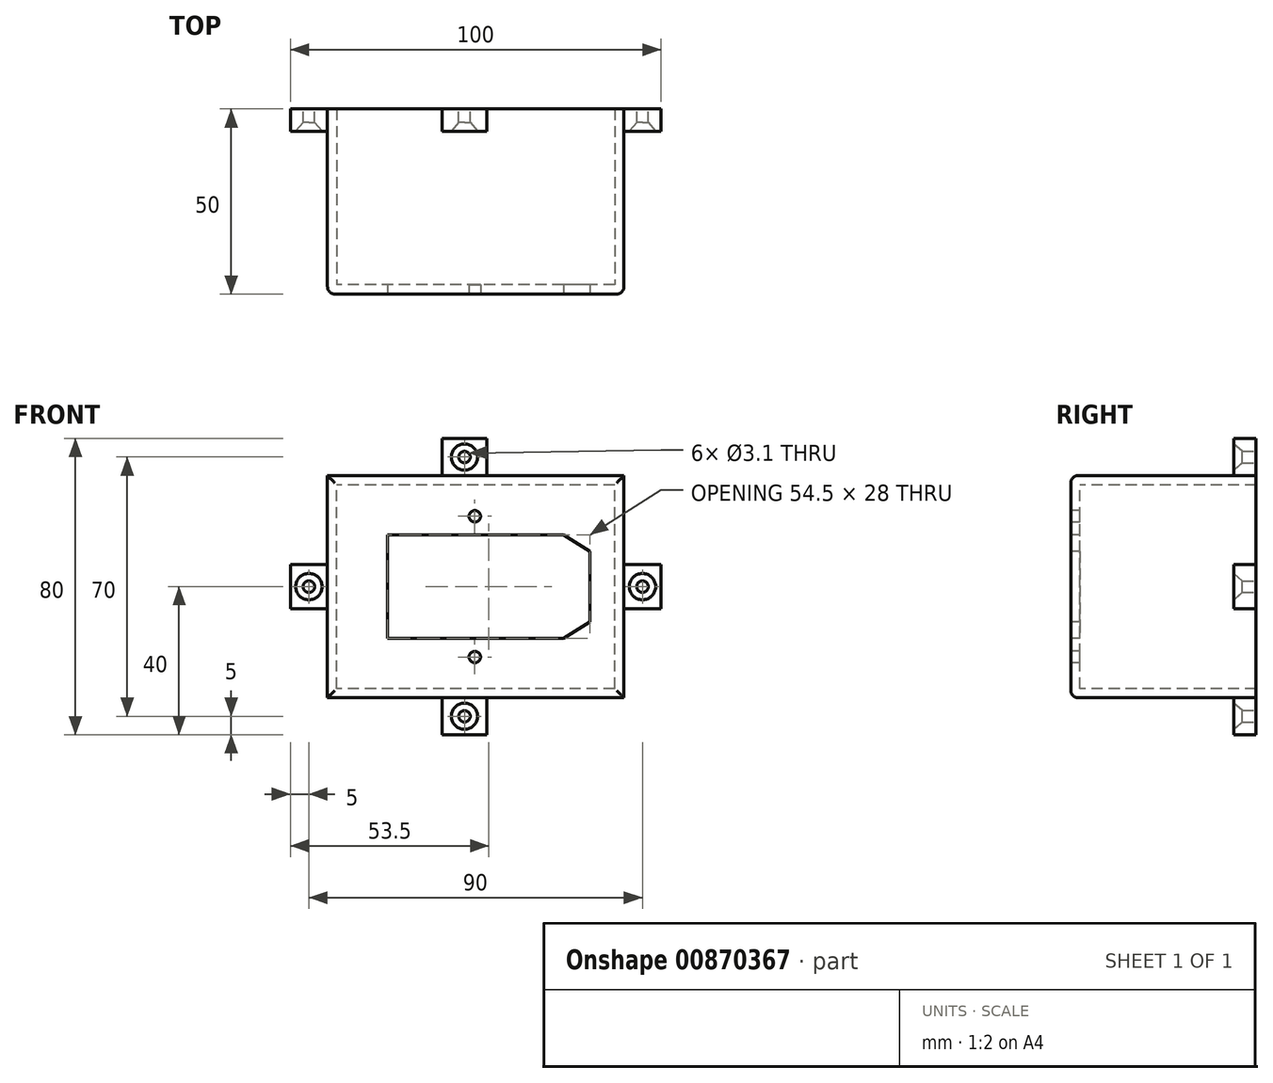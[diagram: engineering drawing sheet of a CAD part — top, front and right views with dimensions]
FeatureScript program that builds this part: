
annotation { "Feature Type Name" : "Feature", "Feature Type Description" : "" }
export const myFeature = defineFeature(function(context is Context, id is Id, definition is map)
    precondition{}
    {
        {
            var Q0;
            Q0=qCreatedBy(makeId("Front.planeOp"),FACE);
            var sketch = newSketch(context, id + "F0", { "sketchPlane" : qUnion([Q0])});
            skLineSegment(sketch, "E0.bottom", {"start": v(40, -30) * mm, "end": v(-40, -30) * mm});
            skLineSegment(sketch, "E0.top", {"start": v(40, 30) * mm, "end": v(-40, 30) * mm});
            skLineSegment(sketch, "E0.left", {"start": v(40, -30) * mm, "end": v(40, 30) * mm});
            skLineSegment(sketch, "E0.right", {"start": v(-40, -30) * mm, "end": v(-40, 30) * mm});
            skPoint(sketch, "E0.middle", {"position": v(0, 0) * mm});
            skLineSegment(sketch, "E1.bottom", {"start": v(23.75, -14) * mm, "end": v(-23.75, -14) * mm});
            skLineSegment(sketch, "E1.top", {"start": v(23.75, 14) * mm, "end": v(-23.75, 14) * mm});
            skLineSegment(sketch, "E1.left", {"start": v(23.75, -14) * mm, "end": v(23.75, 14) * mm});
            skLineSegment(sketch, "E1.right", {"start": v(-23.75, -14) * mm, "end": v(-23.75, 14) * mm});
            skLineSegment(sketch, "E2", {"start": v(30.75, 9.5) * mm, "end": v(30.75, -9.5) * mm});
            skLineSegment(sketch, "E3", {"start": v(30.75, -9.5) * mm, "end": v(23.75, -14) * mm});
            skLineSegment(sketch, "E4", {"start": v(30.75, 9.5) * mm, "end": v(23.75, 14) * mm});
            skLineSegment(sketch, "E5.0", {"start": v(37.5, -27.5) * mm, "end": v(-37.5, -27.5) * mm});
            skLineSegment(sketch, "E5.1", {"start": v(37.5, -27.5) * mm, "end": v(37.5, 27.5) * mm});
            skLineSegment(sketch, "E5.2", {"start": v(37.5, 27.5) * mm, "end": v(-37.5, 27.5) * mm});
            skLineSegment(sketch, "E5.3", {"start": v(-37.5, -27.5) * mm, "end": v(-37.5, 27.5) * mm});
            skCircle(sketch, "E6", {"center": v(-0.25, 19) * mm, "radius": 1.55 * mm});
            skPoint(sketch, "E6.centerSnap0", {"position": v(0, 14) * mm});
            skCircle(sketch, "E7.MirrorC", {"center": v(-0.25, -19) * mm, "radius": 1.55 * mm});
            skSolve(sketch);
        }
        {
            var Q0;
            Q0=qSketchRegion(id+"F0",true);
            extrude(context, id + "F1", {"entities" : qUnion([Q0]), "oppositeDirection" : true, "depth" : 50 * mm, "offsetDistance" : 25 * mm});
        }
        {
            var Q0;
            Q0=makeQuery(id+"F0.imprint","IMPRINT",FACE,{"disambiguationData":[TD([[makeQuery(id+"F0.imprint","IMPRINT",EDGE,{"derivedFrom":sQuery(id+"F0.wireOp",EDGE,"E1.bottom")}),1.0]])]});
            extrude(context, id + "F2", {"entities" : qUnion([Q0]), "operationType" : NewBodyOperationType.ADD, "oppositeDirection" : true, "depth" : 2.5 * mm, "offsetDistance" : 25 * mm});
        }
        {
            var Q0;
            Q0=makeQuery(id+"F1.opExtrude","CAP_FACE",FACE,{"disambiguationData":[OSD([sQuery(id+"F0.wireOp",EDGE,"E0.bottom"),sQuery(id+"F0.wireOp",EDGE,"E0.top"),sQuery(id+"F0.wireOp",EDGE,"E0.left"),sQuery(id+"F0.wireOp",EDGE,"E0.right"),sQuery(id+"F0.wireOp",EDGE,"E5.0"),sQuery(id+"F0.wireOp",EDGE,"E5.1"),sQuery(id+"F0.wireOp",EDGE,"E5.2"),sQuery(id+"F0.wireOp",EDGE,"E5.3")])],"isStart":false});
            var sketch = newSketch(context, id + "F3", { "sketchPlane" : qUnion([Q0])});
            skLineSegment(sketch, "E8.bottom", {"start": v(40, -6) * mm, "end": v(50, -6) * mm});
            skLineSegment(sketch, "E8.top", {"start": v(40, 6) * mm, "end": v(50, 6) * mm});
            skLineSegment(sketch, "E8.left", {"start": v(40, -6) * mm, "end": v(40, 6) * mm});
            skLineSegment(sketch, "E8.right", {"start": v(50, -6) * mm, "end": v(50, 6) * mm});
            skCircle(sketch, "E9", {"center": v(45, 0) * mm, "radius": 1.55 * mm});
            skLineSegment(sketch, "E10.MirrorCS", {"start": v(-50, -6) * mm, "end": v(-50, 6) * mm});
            skCircle(sketch, "E11.MirrorC", {"center": v(-45, 0) * mm, "radius": 1.55 * mm});
            skLineSegment(sketch, "E12.MirrorCS", {"start": v(-40, -6) * mm, "end": v(-50, -6) * mm});
            skLineSegment(sketch, "E13.MirrorCS", {"start": v(-40, -6) * mm, "end": v(-40, 6) * mm});
            skLineSegment(sketch, "E14.MirrorCS", {"start": v(-40, 6) * mm, "end": v(-50, 6) * mm});
            skLineSegment(sketch, "E15.bottom", {"start": v(-2.98, -40) * mm, "end": v(9.02, -40) * mm});
            skLineSegment(sketch, "E15.top", {"start": v(-2.98, -30) * mm, "end": v(9.02, -30) * mm});
            skLineSegment(sketch, "E15.left", {"start": v(-2.98, -40) * mm, "end": v(-2.98, -30) * mm});
            skLineSegment(sketch, "E15.right", {"start": v(9.02, -40) * mm, "end": v(9.02, -30) * mm});
            skCircle(sketch, "E16", {"center": v(3.02, -35) * mm, "radius": 1.55 * mm});
            skLineSegment(sketch, "E17.MirrorCS", {"start": v(9.02, 40) * mm, "end": v(9.02, 30) * mm});
            skLineSegment(sketch, "E18.MirrorCS", {"start": v(-2.98, 40) * mm, "end": v(-2.98, 30) * mm});
            skLineSegment(sketch, "E19.MirrorCS", {"start": v(-2.98, 40) * mm, "end": v(9.02, 40) * mm});
            skLineSegment(sketch, "E20.MirrorCS", {"start": v(-2.98, 30) * mm, "end": v(9.02, 30) * mm});
            skCircle(sketch, "E21.MirrorC", {"center": v(3.02, 35) * mm, "radius": 1.55 * mm});
            skSolve(sketch);
        }
        {
            var Q0;
            Q0=makeQuery(id+"F3.imprint","IMPRINT",FACE,{"disambiguationData":[TD([[makeQuery(id+"F3.imprint","IMPRINT",EDGE,{"derivedFrom":sQuery(id+"F3.wireOp",EDGE,"E8.bottom")}),1.0]])]});
            var Q1;
            Q1=makeQuery(id+"F3.imprint","IMPRINT",FACE,{"disambiguationData":[TD([[makeQuery(id+"F3.imprint","IMPRINT",EDGE,{"derivedFrom":sQuery(id+"F3.wireOp",EDGE,"E15.bottom")}),1.0]])]});
            var Q2;
            Q2=makeQuery(id+"F3.imprint","IMPRINT",FACE,{"disambiguationData":[TD([[makeQuery(id+"F3.imprint","IMPRINT",EDGE,{"derivedFrom":sQuery(id+"F3.wireOp",EDGE,"E13.MirrorCS")}),1.0]])]});
            var Q3;
            Q3=makeQuery(id+"F3.imprint","IMPRINT",FACE,{"disambiguationData":[TD([[makeQuery(id+"F3.imprint","IMPRINT",EDGE,{"derivedFrom":sQuery(id+"F3.wireOp",EDGE,"E17.MirrorCS")}),-1.0]])]});
            extrude(context, id + "F4", {"entities" : qUnion([Q0, Q1, Q2, Q3]), "operationType" : NewBodyOperationType.ADD, "oppositeDirection" : true, "depth" : 6 * mm, "offsetDistance" : 25 * mm});
        }
        {
            var Q0;
            Q0=makeQuery(id+"F1.opExtrude","CAP_EDGE",EDGE,{"disambiguationData":[OSD([sQuery(id+"F0.wireOp",EDGE,"E0.left")])],"isStart":true});
            var Q1;
            Q1=makeQuery(id+"F1.opExtrude","CAP_EDGE",EDGE,{"disambiguationData":[OSD([sQuery(id+"F0.wireOp",EDGE,"E0.right")])],"isStart":true});
            var Q2;
            Q2=makeQuery(id+"F1.opExtrude","CAP_EDGE",EDGE,{"disambiguationData":[OSD([sQuery(id+"F0.wireOp",EDGE,"E0.top")])],"isStart":true});
            var Q3;
            Q3=makeQuery(id+"F1.opExtrude","CAP_EDGE",EDGE,{"disambiguationData":[OSD([sQuery(id+"F0.wireOp",EDGE,"E0.bottom")])],"isStart":true});
            fillet(context, id + "F5", {"entities" : qUnion([Q0, Q1, Q2, Q3]), "radius" : 2 * mm, "tangentPropagation" : true, "allowEdgeOverflow" : false});
        }
        {
            var Q0;
            Q0=makeQuery(id+"F4.opExtrude","CAP_FACE",FACE,{"disambiguationData":[OSD([sQuery(id+"F3.wireOp",EDGE,"E15.bottom"),sQuery(id+"F3.wireOp",EDGE,"E15.top"),sQuery(id+"F3.wireOp",EDGE,"E15.left"),sQuery(id+"F3.wireOp",EDGE,"E15.right"),sQuery(id+"F3.wireOp",EDGE,"E16")])],"isStart":false});
            var sketch = newSketch(context, id + "F6", { "sketchPlane" : qUnion([Q0])});
            skPoint(sketch, "E22", {"position": v(-3.02, -35) * mm});
            skSolve(sketch);
        }
        {
            var Q0;
            Q0=makeQuery(id+"F4.opExtrude","CAP_FACE",FACE,{"disambiguationData":[OSD([sQuery(id+"F3.wireOp",EDGE,"E17.MirrorCS"),sQuery(id+"F3.wireOp",EDGE,"E18.MirrorCS"),sQuery(id+"F3.wireOp",EDGE,"E19.MirrorCS"),sQuery(id+"F3.wireOp",EDGE,"E20.MirrorCS"),sQuery(id+"F3.wireOp",EDGE,"E21.MirrorC")])],"isStart":false});
            var sketch = newSketch(context, id + "F7", { "sketchPlane" : qUnion([Q0])});
            skPoint(sketch, "E23", {"position": v(-3.02, 35) * mm});
            skSolve(sketch);
        }
        {
            var Q0;
            Q0=makeQuery(id+"F4.opExtrude","CAP_FACE",FACE,{"disambiguationData":[OSD([sQuery(id+"F3.wireOp",EDGE,"E13.MirrorCS"),sQuery(id+"F3.wireOp",EDGE,"E11.MirrorC"),sQuery(id+"F3.wireOp",EDGE,"E10.MirrorCS"),sQuery(id+"F3.wireOp",EDGE,"E14.MirrorCS"),sQuery(id+"F3.wireOp",EDGE,"E12.MirrorCS")])],"isStart":false});
            var sketch = newSketch(context, id + "F8", { "sketchPlane" : qUnion([Q0])});
            skPoint(sketch, "E24", {"position": v(45, 0) * mm});
            skSolve(sketch);
        }
        {
            var Q0;
            Q0=makeQuery(id+"F4.opExtrude","CAP_FACE",FACE,{"disambiguationData":[OSD([sQuery(id+"F3.wireOp",EDGE,"E8.bottom"),sQuery(id+"F3.wireOp",EDGE,"E8.top"),sQuery(id+"F3.wireOp",EDGE,"E8.left"),sQuery(id+"F3.wireOp",EDGE,"E8.right"),sQuery(id+"F3.wireOp",EDGE,"E9")])],"isStart":false});
            var sketch = newSketch(context, id + "F9", { "sketchPlane" : qUnion([Q0])});
            skPoint(sketch, "E25", {"position": v(-45, 0) * mm});
            skSolve(sketch);
        }
        {
            var Q0;
            Q0=sQuery(id+"F6.wireOp",VERTEX,"E22");
            var Q1;
            Q1=sQuery(id+"F7.wireOp",VERTEX,"E23");
            var Q2;
            Q2=sQuery(id+"F9.wireOp",VERTEX,"E25");
            var Q3;
            Q3=sQuery(id+"F8.wireOp",VERTEX,"E24");
            var Q4;
            Q4=makeQuery(id+"F1.opExtrude","SWEPT_BODY",BODY,{"disambiguationData":[OSD([sQuery(id+"F0.wireOp",EDGE,"E0.bottom"),sQuery(id+"F0.wireOp",EDGE,"E0.top"),sQuery(id+"F0.wireOp",EDGE,"E0.left"),sQuery(id+"F0.wireOp",EDGE,"E0.right"),sQuery(id+"F0.wireOp",EDGE,"E5.0"),sQuery(id+"F0.wireOp",EDGE,"E5.1"),sQuery(id+"F0.wireOp",EDGE,"E5.2"),sQuery(id+"F0.wireOp",EDGE,"E5.3")])]});
            hole(context, id + "F10", {"style" : HoleStyle.C_SINK, "endStyle" : HoleEndStyle.THROUGH, "holeDiameter" : 3.1 * mm, "cSinkDiameter" : 7.1 * mm, "cSinkAngle" : 82 * degree, "majorDiameter" : 5 * mm, "isTappedThrough" : true, "tappedDepth" : 12 * mm, "tapClearance" : 3, "locations" : qUnion([Q0, Q1, Q2, Q3]), "scope" : qUnion([Q4])});
        }
    });
